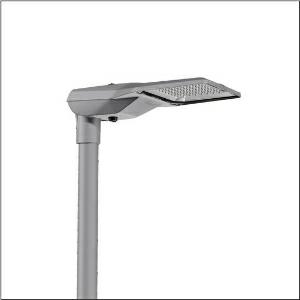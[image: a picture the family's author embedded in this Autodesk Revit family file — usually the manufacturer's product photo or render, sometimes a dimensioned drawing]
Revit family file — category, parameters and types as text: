
# Revit family: streetlight_sl_21_midi___st0_5a_5xe3b33t08lb_a6fa
name_source: partatom
category: Lighting Fixtures
units: mm (PartAtom-declared; Revit-internal decimal feet)

## family parameters
Cut with Voids When Loaded = No
Host = Face
Light Source = No
Part Type = Normal
Room Calculation Point = No
Round Connector Dimension = Use Diameter
Shared = No

## types (1)
- --- (1 x LED, 14340 lm, 99.6 W, 3000K)
    Apparent Load = 100 VA
    CIE Flux Codes = 41 75 97 100 100
    Color Rendering = 70
    Color Temperature = 3000K
    Default Elevation = 1800 mm
    Description = Streetlight SL 21 midi, mast luminaire, primary light control with lens, of PMMA, primary optical cover: cover, of toughened safety glass, transparent, light distribution: ST0.5a, light emission: direct distribution, primary light characteristic: asymmetric, installation type: side-entry, post-top, LED, High Power LED, rated luminous flux: 14.340lm, luminous efficacy: 144lm/W, light colour: 730, colour temperature: 3000K, control gear: D4i, control: overheat protection, constant luminous flux control, time-dependent luminous flux control, flexible luminous flux parameterisation, pre-setting: logarithmic dimming characteristic, mains connection: 230..240V, AC, 50/60Hz, start of lifetime: 100W, end of service life: 102W, reduction: 46W, luminaire housing, of diecast aluminium, powder-coated, SITECO metallic grey (DB 702S), corrosivity category C5 high according to DIN EN ISO 12944, please order mast flange separately, inclination adjustable: 0°, 5°, 10°, 15°, sealing non-destructively replaceable, multi-level sealing system, length: 644mm, width: 335mm, height: 110mm, mast flange for spigot size: 42mm (side-entry): 5XC10008XM4, 60/48mm (side-entry/post-top): 5XC10108XM2, 76/60mm (side-entry/post-top): 5XC10108XM1, mounting height: 4..8m, Smart Interface below and above, protection rating (complete): IP66, insulation class (complete): insulation class II (safety insulation), certification: CE, ENEC, ENEC+, VDE, impact resistance: IK10, permissible operating ambient temperature for outdoor applications: -40..+50°C, standard-compliant lighting for roads and squares, packaging unit: 1 piece

Light Distribution: ST0.5a
    Height = 111 mm
    Lamp = 1 x LED
    Lamp Light Flux = 14340 lm
    Lamp Power = 99.6 W
    Lamp count = 1
    Length = 644 mm
    Luminous efficacy = 144 lm/W
    Manufacturer = Siteco
    ModVariant = No
    Model = 5XE3B33T08LB
    Number of Poles = 1
    OnlyDefault = Yes
    Power Factor = 1
    Product Name = Streetlight SL 21 midi | ST0.5a
    Product group = mast luminaire | pylon top
    ProductGroupID = 6100
    Protection Class = Protection class II
    Protection Degree = IP 66
    RLX_Detail_Level = 1
    RLX_Emergency_Light_Flux = 0 lm
    RLX_Emergency_Type = 0
    RLX_Emergency_Type_DB = No
    RlxData = <blob elided: 38053 chars, md5=f71bb6fa>
    Socket = socket
    Standby Power = 0 W
    System Light Flux = 14340 lm
    System Power = 100 W
    Type Comments = factory setting: luminous flux: 100 % | dim-lin: 254 | 1020 mA
    Type Image = l_1004304.jpg
    URL = http://relux.com
    VarID = @adj_032223
    Voltage = 0 V
    Weight = 0.00 kg
    Width = 336 mm

## geometry (parser evidence)
native form markers: Blend x4, Sweep x11
no freeform markers — native parametric forms only
